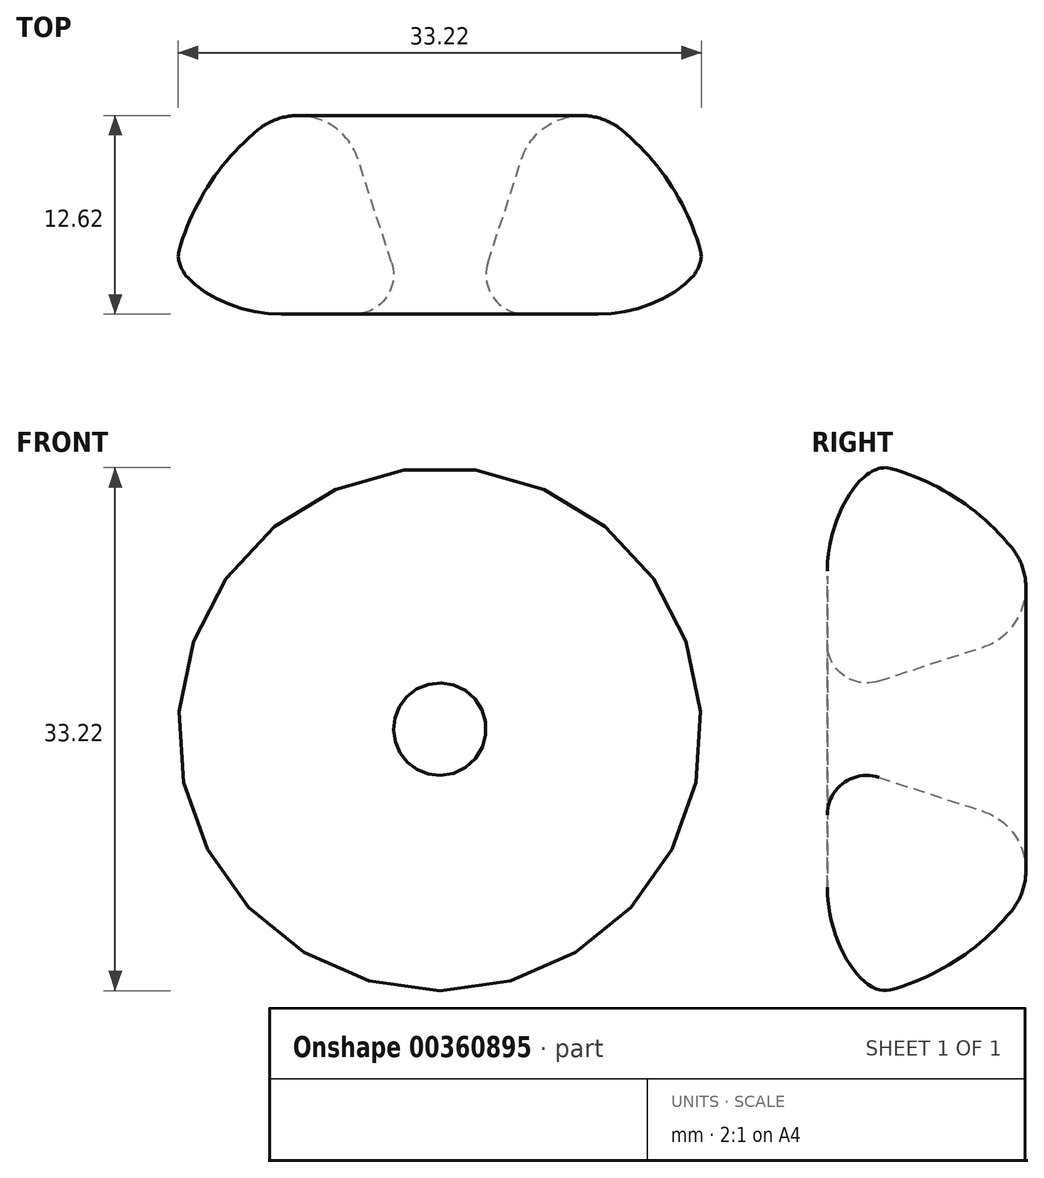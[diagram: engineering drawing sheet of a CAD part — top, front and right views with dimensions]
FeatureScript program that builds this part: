
annotation { "Feature Type Name" : "Feature", "Feature Type Description" : "" }
export const myFeature = defineFeature(function(context is Context, id is Id, definition is map)
    precondition{}
    {
        {
            var Q0;
            Q0=qCreatedBy(makeId("Top.planeOp"),FACE);
            var sketch = newSketch(context, id + "F0", { "sketchPlane" : qUnion([Q0])});
            skLineSegment(sketch, "E0", {"start": v(5.44, 0) * mm, "end": v(10.05, 0) * mm});
            skLineSegment(sketch, "E1", {"start": v(0, 0) * mm, "end": v(0, 6.95) * mm});
            skPoint(sketch, "E2.visualSharp", {"position": v(0, 0) * mm});
            skLineSegment(sketch, "E3", {"start": v(0, 0) * mm, "end": v(2, 0) * mm});
            skLineSegment(sketch, "E4", {"start": v(3.06, 3.27) * mm, "end": v(5.2, 9.85) * mm});
            skArc(sketch, "E5", {"start": v(16.56, 4.01) * mm, "mid": v(14.65, 8.26) * mm, "end": v(11.53, 11.72) * mm});
            skPoint(sketch, "E6.newPointB", {"position": v(0.1, 0) * mm});
            skArc(sketch, "E6.filletArc", {"start": v(3.06, 3.27) * mm, "mid": v(3.42, 1.03) * mm, "end": v(5.44, 0) * mm});
            skEllipticalArc(sketch, "E7", {});
            skPoint(sketch, "E8.orphan", {"position": v(17.1, 0) * mm});
            skPoint(sketch, "E9.visualSharp", {"position": v(6.67, 14.36) * mm});
            skArc(sketch, "E9.filletArc", {"start": v(11.53, 11.72) * mm, "mid": v(7.87, 12.45) * mm, "end": v(5.2, 9.85) * mm});
            skLineSegment(sketch, "E10", {"start": v(3.06, 3.27) * mm, "end": v(16.55, 3.27) * mm});
            const initialGuessF0  = {"E7": [0.011728588211785879, 0.0027295478763953137, 0.967459033150678, 0.25302770436289274, 0.005, 0.0025, 4.230450797847677, 0.00646525296115315]};
            skSetInitialGuess(sketch, initialGuessF0);
            skSolve(sketch);
        }
        {
            var Q0;
            Q0 = qSketchRegion(id + "F0", true);
            var Q1;
            Q1=sQuery(id+"F0.wireOp",EDGE,"E1");
            revolve(context, id + "F1", {"entities" : qUnion([Q0]), "axis" : qUnion([Q1]), "revolveType" : RevolveType.FULL});
        }
    });
